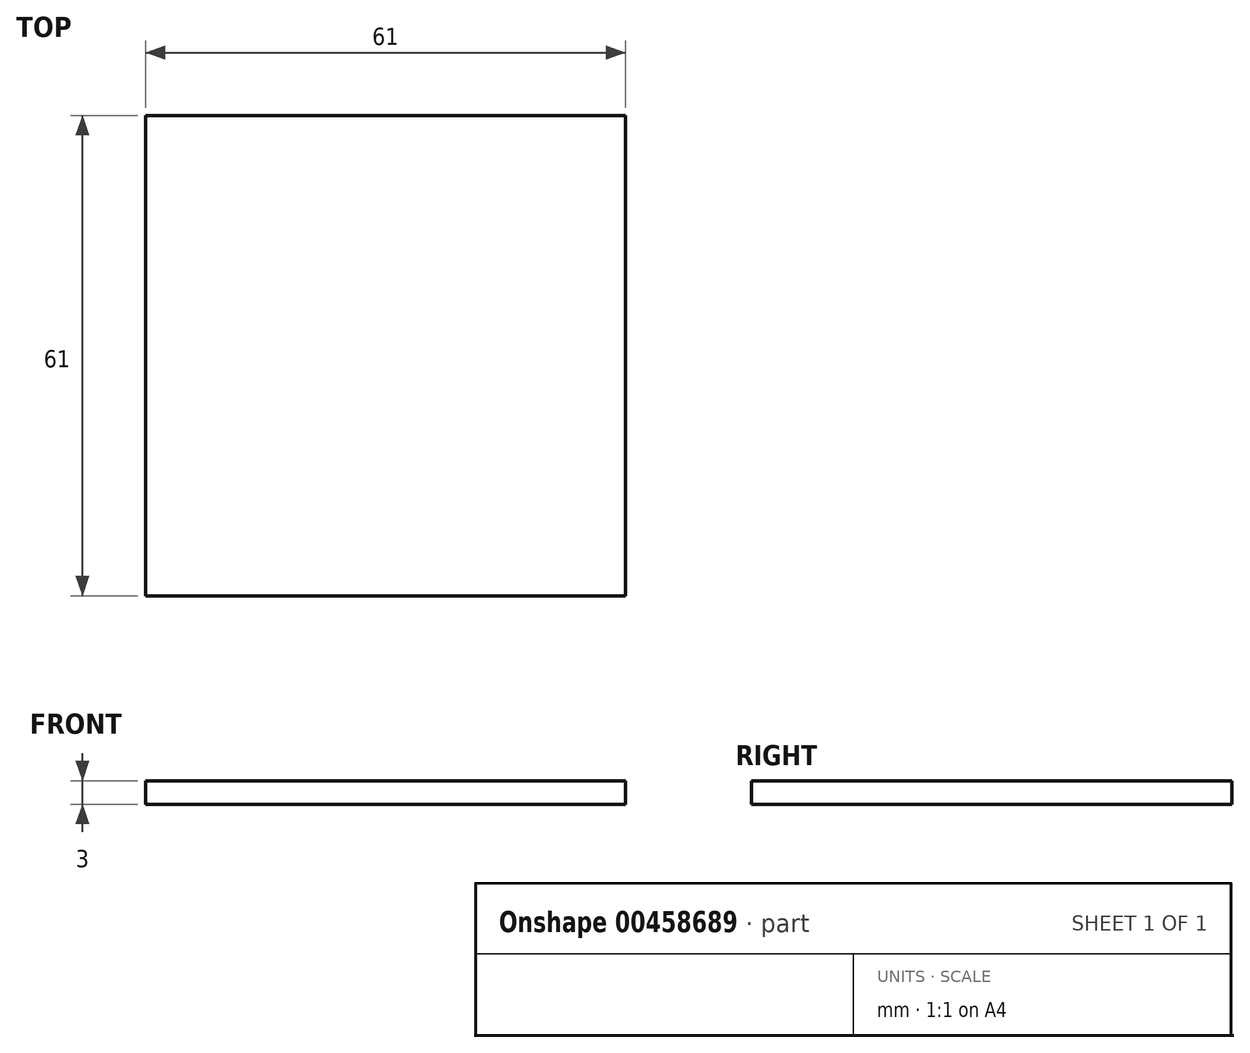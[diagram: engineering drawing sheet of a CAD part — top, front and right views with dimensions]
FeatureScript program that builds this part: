
annotation { "Feature Type Name" : "Feature", "Feature Type Description" : "" }
export const myFeature = defineFeature(function(context is Context, id is Id, definition is map)
    precondition{}
    {
        {
            var Q0;
            Q0=qCreatedBy(makeId("Top.planeOp"),FACE);
            var sketch = newSketch(context, id + "F0", { "sketchPlane" : qUnion([Q0])});
            skSolve(sketch);
        }
        {
            var Q0;
            Q0=qCreatedBy(makeId("Top.planeOp"),FACE);
            var sketch = newSketch(context, id + "F1", { "sketchPlane" : qUnion([Q0])});
            skLineSegment(sketch, "E0.bottom", {"start": v(-32.06, 31.45) * mm, "end": v(28.94, 31.45) * mm});
            skLineSegment(sketch, "E0.top", {"start": v(-32.06, -29.55) * mm, "end": v(28.94, -29.55) * mm});
            skLineSegment(sketch, "E0.left", {"start": v(-32.06, 31.45) * mm, "end": v(-32.06, -29.55) * mm});
            skLineSegment(sketch, "E0.right", {"start": v(28.94, 31.45) * mm, "end": v(28.94, -29.55) * mm});
            skSolve(sketch);
        }
        {
            var Q0;
            Q0=makeQuery(id+"F1.imprint","IMPRINT",FACE,{"disambiguationData":[TD([[makeQuery(id+"F1.imprint","IMPRINT",EDGE,{"derivedFrom":sQuery(id+"F1.wireOp",EDGE,"E0.bottom")}),-1.0]])]});
            extrude(context, id + "F2", {"entities" : qUnion([Q0]), "depth" : 3 * mm, "offsetDistance" : 25 * mm});
        }
    });
